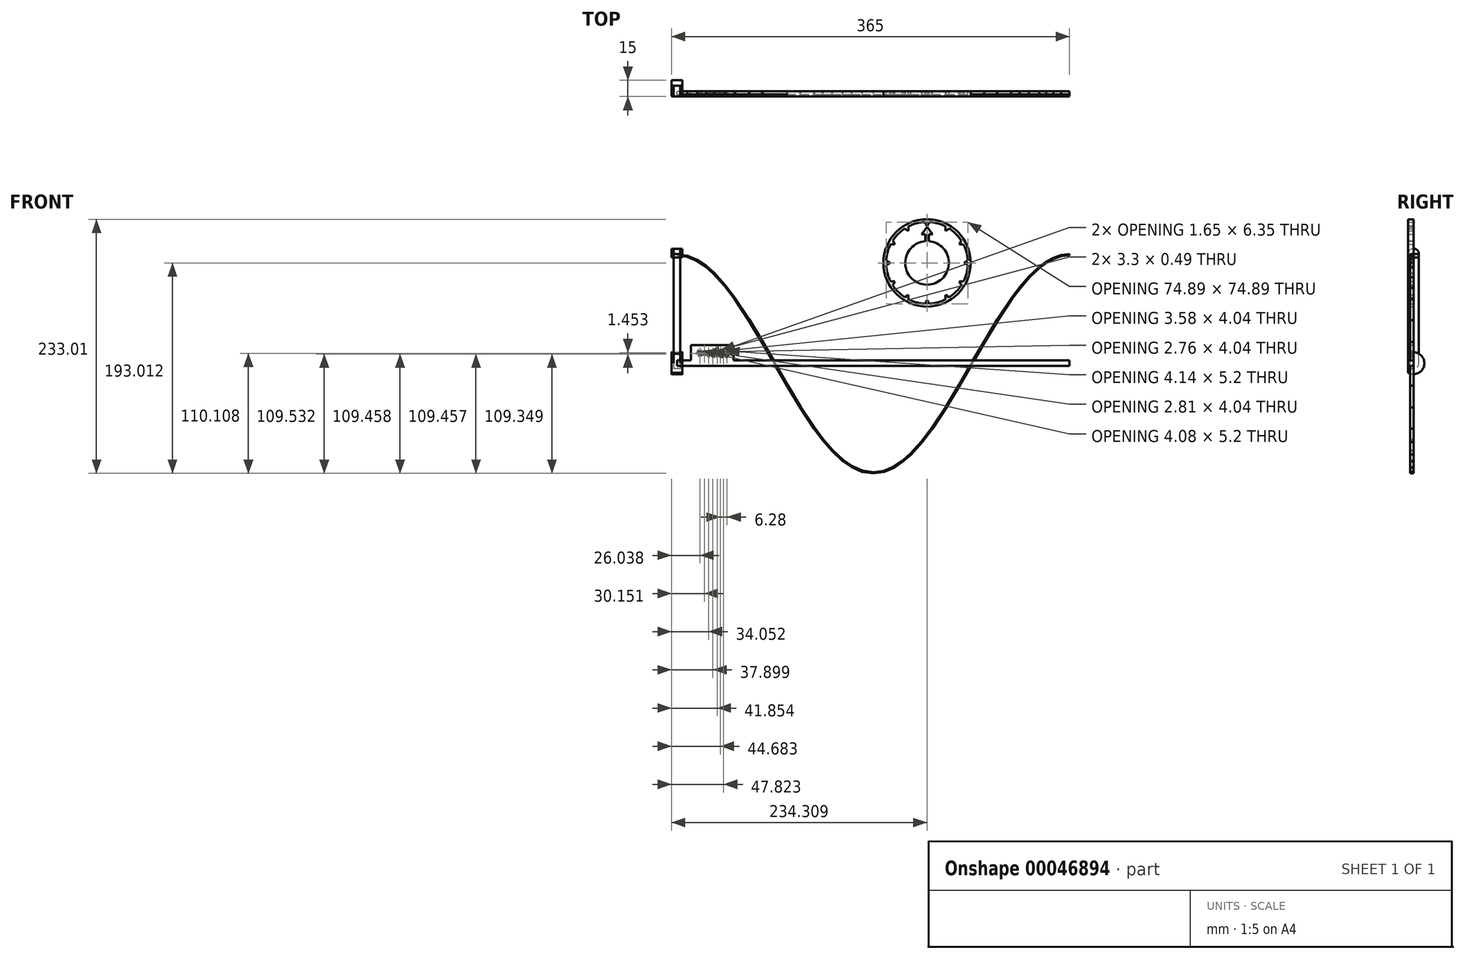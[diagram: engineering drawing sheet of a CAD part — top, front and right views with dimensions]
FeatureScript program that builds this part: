
annotation { "Feature Type Name" : "Feature", "Feature Type Description" : "" }
export const myFeature = defineFeature(function(context is Context, id is Id, definition is map)
    precondition{}
    {
        {
            var Q0;
            Q0=qCreatedBy(makeId("Right.planeOp"),FACE);
            var sketch = newSketch(context, id + "F0", { "sketchPlane" : qUnion([Q0])});
            skArc(sketch, "E0", {"start": v(-5, 0) * mm, "mid": v(0, -5) * mm, "end": v(5, 0) * mm});
            skArc(sketch, "E1", {"start": v(5, 100) * mm, "mid": v(0, 105) * mm, "end": v(-5, 100) * mm});
            skLineSegment(sketch, "E2.left", {"start": v(5, 0) * mm, "end": v(5, 100) * mm});
            skLineSegment(sketch, "E2.right", {"start": v(-5, 0) * mm, "end": v(-5, 100) * mm});
            skSolve(sketch);
        }
        {
            var Q0;
            Q0 = qSketchRegion(id + "F0", true);
            extrude(context, id + "F1", {"entities" : qUnion([Q0]), "endBound" : BoundingType.SYMMETRIC, "depth" : 6 * mm});
        }
        {
            var Q0;
            Q0=qCreatedBy(makeId("Right.planeOp"),FACE);
            var sketch = newSketch(context, id + "F2", { "sketchPlane" : qUnion([Q0])});
            skArc(sketch, "E3", {"start": v(5, 100) * mm, "mid": v(0, 105) * mm, "end": v(-5, 100) * mm});
            skLineSegment(sketch, "E4", {"start": v(5, 100) * mm, "end": v(-5, 100) * mm});
            skSolve(sketch);
        }
        {
            var Q0;
            Q0 = qSketchRegion(id + "F2", true);
            extrude(context, id + "F3", {"entities" : qUnion([Q0]), "endBound" : BoundingType.SYMMETRIC, "depth" : 10 * mm});
        }
        {
            var Q0;
            Q0=qCreatedBy(makeId("Right.planeOp"),FACE);
            var sketch = newSketch(context, id + "F4", { "sketchPlane" : qUnion([Q0])});
            skLineSegment(sketch, "E5.top", {"start": v(5, 97) * mm, "end": v(-5, 97) * mm});
            skLineSegment(sketch, "E5.left", {"start": v(5, 100) * mm, "end": v(5, 97) * mm});
            skLineSegment(sketch, "E5.right", {"start": v(-5, 100) * mm, "end": v(-5, 97) * mm});
            skLineSegment(sketch, "E6", {"start": v(-5, 100) * mm, "end": v(5, 100) * mm});
            skPoint(sketch, "E5.bottom.end.orphan", {"position": v(-5, 103) * mm});
            skPoint(sketch, "E5.bottom.start.orphan", {"position": v(5, 103) * mm});
            skSolve(sketch);
        }
        {
            var Q0;
            Q0 = qSketchRegion(id + "F4", true);
            extrude(context, id + "F5", {"entities" : qUnion([Q0]), "endBound" : BoundingType.SYMMETRIC, "depth" : 10 * mm});
        }
        {
            var Q0;
            Q0=qCreatedBy(makeId("Right.planeOp"),FACE);
            var sketch = newSketch(context, id + "F6", { "sketchPlane" : qUnion([Q0])});
            skArc(sketch, "E7", {"start": v(-5, -8.66) * mm, "mid": v(10, 0) * mm, "end": v(-5, 8.66) * mm});
            skLineSegment(sketch, "E8", {"start": v(-5, 8.66) * mm, "end": v(-5, -8.66) * mm});
            skSolve(sketch);
        }
        {
            var Q0;
            Q0 = qSketchRegion(id + "F6", true);
            extrude(context, id + "F7", {"entities" : qUnion([Q0]), "endBound" : BoundingType.SYMMETRIC, "depth" : 10 * mm});
        }
        {
            var Q0;
            Q0=qCreatedBy(makeId("Front.planeOp"),FACE);
            var sketch = newSketch(context, id + "F8", { "sketchPlane" : qUnion([Q0])});
            skLineSegment(sketch, "E9.bottom", {"start": v(0, 2.5) * mm, "end": v(12.73, 2.5) * mm});
            skLineSegment(sketch, "E9.top", {"start": v(0, -2.5) * mm, "end": v(360, -2.5) * mm});
            skLineSegment(sketch, "E9.left", {"start": v(0, 2.5) * mm, "end": v(0, -2.5) * mm});
            skLineSegment(sketch, "E9.right", {"start": v(360, 2.5) * mm, "end": v(360, -2.5) * mm});
            skLineSegment(sketch, "E10.bottom", {"start": v(12.73, 16.53) * mm, "end": v(51.84, 16.53) * mm});
            skLineSegment(sketch, "E10.left", {"start": v(12.73, 16.53) * mm, "end": v(12.73, 2.5) * mm});
            skLineSegment(sketch, "E10.right", {"start": v(51.84, 16.53) * mm, "end": v(51.84, 2.5) * mm});
            skText(sketch, "E11", { "text": "Y=cos(X)\n", "fontName": "OpenSans-Regular.ttf"});
            skLineSegment(sketch, "E12.trimOffspring", {"start": v(51.84, 2.5) * mm, "end": v(360, 2.5) * mm});
            const initialGuessF8  = {"E11": [0.019, 0.0065, 1, 0, 0.00524]};
            skSetInitialGuess(sketch, initialGuessF8);
            skSolve(sketch);
        }
        {
            var Q0;
            Q0 = qSketchRegion(id + "F8", true);
            extrude(context, id + "F9", {"entities" : qUnion([Q0]), "depth" : 5 * mm});
        }
        {
            var Q0;
            Q0=qCreatedBy(makeId("Front.planeOp"),FACE);
            var sketch = newSketch(context, id + "F10", { "sketchPlane" : qUnion([Q0])});
            skCircle(sketch, "E13", {"center": v(229.3, 92) * mm, "radius": 40 * mm});
            skArc(sketch, "E14", {"start": v(227.32, 129.45) * mm, "mid": v(219.6, 128.22) * mm, "end": v(212.3, 125.43) * mm});
            skLineSegment(sketch, "E15", {"start": v(229.3, 126) * mm, "end": v(231.3, 129.45) * mm});
            skLineSegment(sketch, "E16", {"start": v(229.3, 126) * mm, "end": v(227.32, 129.45) * mm});
            skLineSegment(sketch, "E17", {"start": v(229.3, 126) * mm, "end": v(229.3, 92) * mm, "construction": true});
            skLineSegment(sketch, "E18.1.0", {"start": v(212.3, 121.45) * mm, "end": v(208.86, 123.44) * mm});
            skLineSegment(sketch, "E18.1.1", {"start": v(212.3, 121.45) * mm, "end": v(212.3, 125.43) * mm});
            skLineSegment(sketch, "E18.2.0", {"start": v(199.86, 109) * mm, "end": v(195.88, 109) * mm});
            skLineSegment(sketch, "E18.2.1", {"start": v(199.86, 109) * mm, "end": v(197.87, 112.45) * mm});
            skLineSegment(sketch, "E18.3.0", {"start": v(195.3, 92) * mm, "end": v(191.86, 90.01) * mm});
            skLineSegment(sketch, "E18.3.1", {"start": v(195.3, 92) * mm, "end": v(191.86, 94) * mm});
            skLineSegment(sketch, "E18.4.0", {"start": v(199.86, 75) * mm, "end": v(197.87, 71.56) * mm});
            skLineSegment(sketch, "E18.4.1", {"start": v(199.86, 75) * mm, "end": v(195.88, 75) * mm});
            skLineSegment(sketch, "E18.5.0", {"start": v(212.3, 62.56) * mm, "end": v(212.3, 58.58) * mm});
            skLineSegment(sketch, "E18.5.1", {"start": v(212.3, 62.56) * mm, "end": v(208.86, 60.57) * mm});
            skLineSegment(sketch, "E18.6.0", {"start": v(229.3, 58) * mm, "end": v(231.3, 54.56) * mm});
            skLineSegment(sketch, "E18.6.1", {"start": v(229.3, 58) * mm, "end": v(227.32, 54.56) * mm});
            skLineSegment(sketch, "E18.7.0", {"start": v(246.3, 62.56) * mm, "end": v(249.76, 60.57) * mm});
            skLineSegment(sketch, "E18.7.1", {"start": v(246.3, 62.56) * mm, "end": v(246.3, 58.58) * mm});
            skLineSegment(sketch, "E18.8.0", {"start": v(258.75, 75) * mm, "end": v(262.73, 75) * mm});
            skLineSegment(sketch, "E18.8.1", {"start": v(258.75, 75) * mm, "end": v(260.74, 71.56) * mm});
            skLineSegment(sketch, "E18.9.0", {"start": v(263.3, 92) * mm, "end": v(266.76, 94) * mm});
            skLineSegment(sketch, "E18.9.1", {"start": v(263.3, 92) * mm, "end": v(266.76, 90.01) * mm});
            skLineSegment(sketch, "E18.10.0", {"start": v(258.75, 109) * mm, "end": v(260.74, 112.45) * mm});
            skLineSegment(sketch, "E18.10.1", {"start": v(258.75, 109) * mm, "end": v(262.73, 109) * mm});
            skLineSegment(sketch, "E18.11.0", {"start": v(246.3, 121.45) * mm, "end": v(246.3, 125.43) * mm});
            skLineSegment(sketch, "E18.11.1", {"start": v(246.3, 121.45) * mm, "end": v(249.76, 123.44) * mm});
            skArc(sketch, "E19.trimOffspring", {"start": v(208.86, 123.44) * mm, "mid": v(202.8, 118.52) * mm, "end": v(197.87, 112.45) * mm});
            skArc(sketch, "E20.trimOffspring", {"start": v(246.3, 125.43) * mm, "mid": v(239.01, 128.22) * mm, "end": v(231.3, 129.45) * mm});
            skArc(sketch, "E21.trimOffspring", {"start": v(260.74, 112.45) * mm, "mid": v(255.83, 118.52) * mm, "end": v(249.76, 123.44) * mm});
            skArc(sketch, "E22.trimOffspring", {"start": v(195.88, 109) * mm, "mid": v(193.09, 101.7) * mm, "end": v(191.86, 94) * mm});
            skArc(sketch, "E23.trimOffspring", {"start": v(191.86, 90.01) * mm, "mid": v(193.09, 82.3) * mm, "end": v(195.88, 75) * mm});
            skArc(sketch, "E24.trimOffspring", {"start": v(266.76, 94) * mm, "mid": v(265.53, 101.7) * mm, "end": v(262.73, 109) * mm});
            skArc(sketch, "E25.trimOffspring", {"start": v(262.73, 75) * mm, "mid": v(265.53, 82.3) * mm, "end": v(266.76, 90.01) * mm});
            skArc(sketch, "E26.trimOffspring", {"start": v(249.76, 60.57) * mm, "mid": v(255.83, 65.49) * mm, "end": v(260.74, 71.56) * mm});
            skArc(sketch, "E27.trimOffspring", {"start": v(231.3, 54.56) * mm, "mid": v(239.01, 55.78) * mm, "end": v(246.3, 58.58) * mm});
            skArc(sketch, "E28.trimOffspring", {"start": v(212.3, 58.58) * mm, "mid": v(219.6, 55.78) * mm, "end": v(227.32, 54.56) * mm});
            skArc(sketch, "E29.trimOffspring", {"start": v(197.87, 71.56) * mm, "mid": v(202.8, 65.49) * mm, "end": v(208.86, 60.57) * mm});
            skLineSegment(sketch, "E30.left", {"start": v(227.8, 111.95) * mm, "end": v(227.8, 118.11) * mm});
            skLineSegment(sketch, "E30.right", {"start": v(230.8, 111.95) * mm, "end": v(230.8, 118.11) * mm});
            skLineSegment(sketch, "E31", {"start": v(229.3, 125) * mm, "end": v(224.3, 118.11) * mm});
            skLineSegment(sketch, "E32", {"start": v(224.3, 118.11) * mm, "end": v(227.8, 118.11) * mm});
            skLineSegment(sketch, "E33", {"start": v(234.3, 118.11) * mm, "end": v(229.3, 125) * mm});
            skLineSegment(sketch, "E34.trimOffspring", {"start": v(230.8, 118.11) * mm, "end": v(234.3, 118.11) * mm});
            skArc(sketch, "E35", {"start": v(227.8, 111.95) * mm, "mid": v(229.3, 72) * mm, "end": v(230.8, 111.95) * mm});
            skSolve(sketch);
        }
        {
            var Q0;
            Q0 = qSketchRegion(id + "F10", true);
            var Q1;
            Q1=makeQuery(id+"F10.imprint","IMPRINT",FACE,{"disambiguationData":[TD([[makeQuery(id+"F10.imprint","IMPRINT",EDGE,{"derivedFrom":sQuery(id+"F10.wireOp",EDGE,"E30.left")}),-1.0]])]});
            extrude(context, id + "F11", {"entities" : qUnion([Q0, Q1]), "depth" : 5 * mm});
        }
        {
            var Q0;
            Q0=qCreatedBy(makeId("Front.planeOp"),FACE);
            var sketch = newSketch(context, id + "F12", { "sketchPlane" : qUnion([Q0])});
            skLineSegment(sketch, "E36", {"start": v(30.91, -2.55) * mm, "end": v(90.38, -2.55) * mm});
            skLineSegment(sketch, "E37", {"start": v(30.91, 97.45) * mm, "end": v(40.53, 96.04) * mm});
            skLineSegment(sketch, "E38", {"start": v(40.53, 96.04) * mm, "end": v(49.5, 92.24) * mm});
            skLineSegment(sketch, "E39", {"start": v(49.5, 92.24) * mm, "end": v(57.58, 86.8) * mm});
            skLineSegment(sketch, "E40", {"start": v(57.58, 86.8) * mm, "end": v(64.9, 80.36) * mm});
            skLineSegment(sketch, "E41", {"start": v(64.9, 80.36) * mm, "end": v(75.2, 69.02) * mm});
            skLineSegment(sketch, "E42", {"start": v(75.2, 69.02) * mm, "end": v(84.49, 56.82) * mm});
            skLineSegment(sketch, "E43", {"start": v(84.49, 56.82) * mm, "end": v(97.32, 37.47) * mm});
            skLineSegment(sketch, "E44", {"start": v(97.32, 37.47) * mm, "end": v(109.3, 17.57) * mm});
            skLineSegment(sketch, "E45", {"start": v(109.3, 17.57) * mm, "end": v(120.91, -2.55) * mm});
            skLineSegment(sketch, "E46", {"start": v(120.91, -2.55) * mm, "end": v(132.52, -22.67) * mm});
            skLineSegment(sketch, "E47", {"start": v(132.52, -22.67) * mm, "end": v(144.5, -42.57) * mm});
            skLineSegment(sketch, "E48", {"start": v(144.5, -42.57) * mm, "end": v(157.33, -61.92) * mm});
            skLineSegment(sketch, "E49", {"start": v(157.33, -61.92) * mm, "end": v(165.15, -72.32) * mm});
            skLineSegment(sketch, "E50", {"start": v(165.15, -72.32) * mm, "end": v(173.66, -82.15) * mm});
            skLineSegment(sketch, "E51", {"start": v(173.66, -82.15) * mm, "end": v(183.15, -91.04) * mm});
            skLineSegment(sketch, "E52", {"start": v(183.15, -91.04) * mm, "end": v(191.52, -96.88) * mm});
            skLineSegment(sketch, "E53", {"start": v(191.52, -96.88) * mm, "end": v(200.84, -101.01) * mm});
            skLineSegment(sketch, "E54", {"start": v(200.84, -101.01) * mm, "end": v(210.91, -102.55) * mm});
            skLineSegment(sketch, "E55", {"start": v(210.91, -102.55) * mm, "end": v(220.53, -101.14) * mm});
            skLineSegment(sketch, "E56", {"start": v(220.53, -101.14) * mm, "end": v(229.5, -97.34) * mm});
            skLineSegment(sketch, "E57", {"start": v(229.5, -97.34) * mm, "end": v(237.58, -91.9) * mm});
            skLineSegment(sketch, "E58", {"start": v(237.58, -91.9) * mm, "end": v(244.9, -85.46) * mm});
            skLineSegment(sketch, "E59", {"start": v(244.9, -85.46) * mm, "end": v(255.2, -74.12) * mm});
            skLineSegment(sketch, "E60", {"start": v(255.2, -74.12) * mm, "end": v(264.49, -61.92) * mm});
            skLineSegment(sketch, "E61", {"start": v(264.49, -61.92) * mm, "end": v(277.32, -42.57) * mm});
            skLineSegment(sketch, "E62", {"start": v(277.32, -42.57) * mm, "end": v(289.3, -22.67) * mm});
            skLineSegment(sketch, "E63", {"start": v(289.3, -22.67) * mm, "end": v(300.91, -2.55) * mm});
            skLineSegment(sketch, "E64", {"start": v(300.91, -2.55) * mm, "end": v(312.52, 17.57) * mm});
            skLineSegment(sketch, "E65", {"start": v(312.52, 17.57) * mm, "end": v(324.5, 37.47) * mm});
            skLineSegment(sketch, "E66", {"start": v(324.5, 37.47) * mm, "end": v(337.33, 56.82) * mm});
            skLineSegment(sketch, "E67", {"start": v(337.33, 56.82) * mm, "end": v(345.15, 67.22) * mm});
            skLineSegment(sketch, "E68", {"start": v(345.15, 67.22) * mm, "end": v(353.66, 77.05) * mm});
            skLineSegment(sketch, "E69", {"start": v(353.66, 77.05) * mm, "end": v(363.15, 85.94) * mm});
            skLineSegment(sketch, "E70", {"start": v(363.15, 85.94) * mm, "end": v(369.34, 90.45) * mm});
            skLineSegment(sketch, "E71", {"start": v(369.34, 90.45) * mm, "end": v(376.07, 94.11) * mm});
            skLineSegment(sketch, "E72", {"start": v(376.07, 94.11) * mm, "end": v(383.31, 96.57) * mm});
            skLineSegment(sketch, "E73", {"start": v(383.31, 96.57) * mm, "end": v(390.91, 97.45) * mm});
            skPoint(sketch, "E74", {"position": v(0, 0) * mm});
            skLineSegment(sketch, "E75", {"start": v(30.91, 97.45) * mm, "end": v(30.91, -2.55) * mm});
            skLineSegment(sketch, "E76", {"start": v(390.91, -2.55) * mm, "end": v(390.91, 97.45) * mm});
            skLineSegment(sketch, "E77.top", {"start": v(90.38, -123.52) * mm, "end": v(342.91, -123.52) * mm});
            skLineSegment(sketch, "E77.left", {"start": v(90.38, -2.55) * mm, "end": v(90.38, -123.52) * mm});
            skLineSegment(sketch, "E77.right", {"start": v(342.91, -2.55) * mm, "end": v(342.91, -123.52) * mm});
            skLineSegment(sketch, "E78.trimOffspring", {"start": v(342.91, -2.55) * mm, "end": v(390.91, -2.55) * mm});
            skSolve(sketch);
        }
        {
            var Q0;
            Q0 = qSketchRegion(id + "F12", true);
            extrude(context, id + "F13", {"entities" : qUnion([Q0]), "depth" : 3 * mm});
        }
        {
            var Q0;
            Q0=makeQuery(id+"F13.opExtrude","SWEPT_BODY",BODY,{"disambiguationData":[OSD([sQuery(id+"F12.wireOp",EDGE,"E36"),sQuery(id+"F12.wireOp",EDGE,"E37"),sQuery(id+"F12.wireOp",EDGE,"E38"),sQuery(id+"F12.wireOp",EDGE,"E39"),sQuery(id+"F12.wireOp",EDGE,"E40"),sQuery(id+"F12.wireOp",EDGE,"E41"),sQuery(id+"F12.wireOp",EDGE,"E42"),sQuery(id+"F12.wireOp",EDGE,"E43"),sQuery(id+"F12.wireOp",EDGE,"E44"),sQuery(id+"F12.wireOp",EDGE,"E45"),sQuery(id+"F12.wireOp",EDGE,"E46"),sQuery(id+"F12.wireOp",EDGE,"E47"),sQuery(id+"F12.wireOp",EDGE,"E48"),sQuery(id+"F12.wireOp",EDGE,"E49"),sQuery(id+"F12.wireOp",EDGE,"E50"),sQuery(id+"F12.wireOp",EDGE,"E51"),sQuery(id+"F12.wireOp",EDGE,"E52"),sQuery(id+"F12.wireOp",EDGE,"E53"),sQuery(id+"F12.wireOp",EDGE,"E54"),sQuery(id+"F12.wireOp",EDGE,"E55"),sQuery(id+"F12.wireOp",EDGE,"E56"),sQuery(id+"F12.wireOp",EDGE,"E57"),sQuery(id+"F12.wireOp",EDGE,"E58"),sQuery(id+"F12.wireOp",EDGE,"E59"),sQuery(id+"F12.wireOp",EDGE,"E60"),sQuery(id+"F12.wireOp",EDGE,"E61"),sQuery(id+"F12.wireOp",EDGE,"E62"),sQuery(id+"F12.wireOp",EDGE,"E63"),sQuery(id+"F12.wireOp",EDGE,"E64"),sQuery(id+"F12.wireOp",EDGE,"E65"),sQuery(id+"F12.wireOp",EDGE,"E66"),sQuery(id+"F12.wireOp",EDGE,"E67"),sQuery(id+"F12.wireOp",EDGE,"E68"),sQuery(id+"F12.wireOp",EDGE,"E69"),sQuery(id+"F12.wireOp",EDGE,"E70"),sQuery(id+"F12.wireOp",EDGE,"E71"),sQuery(id+"F12.wireOp",EDGE,"E72"),sQuery(id+"F12.wireOp",EDGE,"E73"),sQuery(id+"F12.wireOp",EDGE,"E75"),sQuery(id+"F12.wireOp",EDGE,"E76"),sQuery(id+"F12.wireOp",EDGE,"E77.top"),sQuery(id+"F12.wireOp",EDGE,"E77.left"),sQuery(id+"F12.wireOp",EDGE,"E77.right"),sQuery(id+"F12.wireOp",EDGE,"E78.trimOffspring")])]});
            var Q1;
            Q1=makeQuery(id+"F13.opExtrude","CAP_VERTEX",VERTEX,{"disambiguationData":[OSD([sQuery(id+"F12.wireOp",EDGE,"E36"),sQuery(id+"F12.wireOp",EDGE,"E75")])],"isStart":true});
            var Q2;
            Q2=qCreatedBy(makeId("Origin.pointOp"),VERTEX);
            var Q3;
            Q3=makeQuery(id+"F13.opExtrude","CAP_VERTEX",VERTEX,{"disambiguationData":[OSD([sQuery(id+"F12.wireOp",EDGE,"E36"),sQuery(id+"F12.wireOp",EDGE,"E75")])],"isStart":true});
            var Q4;
            Q4=qCreatedBy(makeId("Origin.pointOp"),VERTEX);
            transform(context, id + "F14", {"entities" : qUnion([Q0]), "transformType" : TransformType.TRANSLATION_ENTITY, "oppositeDirectionEntity" : false, "transformLine" : qUnion([Q1, Q2]), "makeCopy" : false});
        }
        {
            var Q0;
            Q0=makeQuery(id+"F13.opExtrude","SWEPT_FACE",FACE,{"disambiguationData":[OSD([sQuery(id+"F12.wireOp",EDGE,"E77.top")])]});
            var Q1;
            Q1=makeQuery(id+"F13.opExtrude","SWEPT_FACE",FACE,{"disambiguationData":[OSD([sQuery(id+"F12.wireOp",EDGE,"E36")])]});
            var Q2;
            Q2=makeQuery(id+"F13.opExtrude","CAP_FACE",FACE,{"disambiguationData":[OSD([sQuery(id+"F12.wireOp",EDGE,"E36"),sQuery(id+"F12.wireOp",EDGE,"E37"),sQuery(id+"F12.wireOp",EDGE,"E38"),sQuery(id+"F12.wireOp",EDGE,"E39"),sQuery(id+"F12.wireOp",EDGE,"E40"),sQuery(id+"F12.wireOp",EDGE,"E41"),sQuery(id+"F12.wireOp",EDGE,"E42"),sQuery(id+"F12.wireOp",EDGE,"E43"),sQuery(id+"F12.wireOp",EDGE,"E44"),sQuery(id+"F12.wireOp",EDGE,"E45"),sQuery(id+"F12.wireOp",EDGE,"E46"),sQuery(id+"F12.wireOp",EDGE,"E47"),sQuery(id+"F12.wireOp",EDGE,"E48"),sQuery(id+"F12.wireOp",EDGE,"E49"),sQuery(id+"F12.wireOp",EDGE,"E50"),sQuery(id+"F12.wireOp",EDGE,"E51"),sQuery(id+"F12.wireOp",EDGE,"E52"),sQuery(id+"F12.wireOp",EDGE,"E53"),sQuery(id+"F12.wireOp",EDGE,"E54"),sQuery(id+"F12.wireOp",EDGE,"E55"),sQuery(id+"F12.wireOp",EDGE,"E56"),sQuery(id+"F12.wireOp",EDGE,"E57"),sQuery(id+"F12.wireOp",EDGE,"E58"),sQuery(id+"F12.wireOp",EDGE,"E59"),sQuery(id+"F12.wireOp",EDGE,"E60"),sQuery(id+"F12.wireOp",EDGE,"E61"),sQuery(id+"F12.wireOp",EDGE,"E62"),sQuery(id+"F12.wireOp",EDGE,"E63"),sQuery(id+"F12.wireOp",EDGE,"E64"),sQuery(id+"F12.wireOp",EDGE,"E65"),sQuery(id+"F12.wireOp",EDGE,"E66"),sQuery(id+"F12.wireOp",EDGE,"E67"),sQuery(id+"F12.wireOp",EDGE,"E68"),sQuery(id+"F12.wireOp",EDGE,"E69"),sQuery(id+"F12.wireOp",EDGE,"E70"),sQuery(id+"F12.wireOp",EDGE,"E71"),sQuery(id+"F12.wireOp",EDGE,"E72"),sQuery(id+"F12.wireOp",EDGE,"E73"),sQuery(id+"F12.wireOp",EDGE,"E75"),sQuery(id+"F12.wireOp",EDGE,"E76"),sQuery(id+"F12.wireOp",EDGE,"E77.top"),sQuery(id+"F12.wireOp",EDGE,"E77.left"),sQuery(id+"F12.wireOp",EDGE,"E77.right"),sQuery(id+"F12.wireOp",EDGE,"E78.trimOffspring")])],"isStart":false});
            var Q3;
            Q3=makeQuery(id+"F13.opExtrude","SWEPT_FACE",FACE,{"disambiguationData":[OSD([sQuery(id+"F12.wireOp",EDGE,"E77.left")])]});
            var Q4;
            Q4=makeQuery(id+"F13.opExtrude","SWEPT_FACE",FACE,{"disambiguationData":[OSD([sQuery(id+"F12.wireOp",EDGE,"E75")])]});
            var Q5;
            Q5=makeQuery(id+"F13.opExtrude","SWEPT_FACE",FACE,{"disambiguationData":[OSD([sQuery(id+"F12.wireOp",EDGE,"E77.right")])]});
            var Q6;
            Q6=makeQuery(id+"F13.opExtrude","SWEPT_FACE",FACE,{"disambiguationData":[OSD([sQuery(id+"F12.wireOp",EDGE,"E78.trimOffspring")])]});
            var Q7;
            Q7=makeQuery(id+"F13.opExtrude","SWEPT_FACE",FACE,{"disambiguationData":[OSD([sQuery(id+"F12.wireOp",EDGE,"E76")])]});
            var Q8;
            Q8=makeQuery(id+"F13.opExtrude","CAP_FACE",FACE,{"disambiguationData":[OSD([sQuery(id+"F12.wireOp",EDGE,"E36"),sQuery(id+"F12.wireOp",EDGE,"E37"),sQuery(id+"F12.wireOp",EDGE,"E38"),sQuery(id+"F12.wireOp",EDGE,"E39"),sQuery(id+"F12.wireOp",EDGE,"E40"),sQuery(id+"F12.wireOp",EDGE,"E41"),sQuery(id+"F12.wireOp",EDGE,"E42"),sQuery(id+"F12.wireOp",EDGE,"E43"),sQuery(id+"F12.wireOp",EDGE,"E44"),sQuery(id+"F12.wireOp",EDGE,"E45"),sQuery(id+"F12.wireOp",EDGE,"E46"),sQuery(id+"F12.wireOp",EDGE,"E47"),sQuery(id+"F12.wireOp",EDGE,"E48"),sQuery(id+"F12.wireOp",EDGE,"E49"),sQuery(id+"F12.wireOp",EDGE,"E50"),sQuery(id+"F12.wireOp",EDGE,"E51"),sQuery(id+"F12.wireOp",EDGE,"E52"),sQuery(id+"F12.wireOp",EDGE,"E53"),sQuery(id+"F12.wireOp",EDGE,"E54"),sQuery(id+"F12.wireOp",EDGE,"E55"),sQuery(id+"F12.wireOp",EDGE,"E56"),sQuery(id+"F12.wireOp",EDGE,"E57"),sQuery(id+"F12.wireOp",EDGE,"E58"),sQuery(id+"F12.wireOp",EDGE,"E59"),sQuery(id+"F12.wireOp",EDGE,"E60"),sQuery(id+"F12.wireOp",EDGE,"E61"),sQuery(id+"F12.wireOp",EDGE,"E62"),sQuery(id+"F12.wireOp",EDGE,"E63"),sQuery(id+"F12.wireOp",EDGE,"E64"),sQuery(id+"F12.wireOp",EDGE,"E65"),sQuery(id+"F12.wireOp",EDGE,"E66"),sQuery(id+"F12.wireOp",EDGE,"E67"),sQuery(id+"F12.wireOp",EDGE,"E68"),sQuery(id+"F12.wireOp",EDGE,"E69"),sQuery(id+"F12.wireOp",EDGE,"E70"),sQuery(id+"F12.wireOp",EDGE,"E71"),sQuery(id+"F12.wireOp",EDGE,"E72"),sQuery(id+"F12.wireOp",EDGE,"E73"),sQuery(id+"F12.wireOp",EDGE,"E75"),sQuery(id+"F12.wireOp",EDGE,"E76"),sQuery(id+"F12.wireOp",EDGE,"E77.top"),sQuery(id+"F12.wireOp",EDGE,"E77.left"),sQuery(id+"F12.wireOp",EDGE,"E77.right"),sQuery(id+"F12.wireOp",EDGE,"E78.trimOffspring")])],"isStart":true});
            shell(context, id + "F15", {"entities" : qUnion([Q0, Q1, Q2, Q3, Q4, Q5, Q6, Q7, Q8]), "thickness" : 1 * mm});
        }
        {
            var Q0;
            Q0=makeQuery(id+"F9.opExtrude","CAP_FACE",FACE,{"disambiguationData":[OSD([sQuery(id+"F8.wireOp",EDGE,"E9.bottom"),sQuery(id+"F8.wireOp",EDGE,"E9.top"),sQuery(id+"F8.wireOp",EDGE,"E9.left"),sQuery(id+"F8.wireOp",EDGE,"E9.right"),sQuery(id+"F8.wireOp",EDGE,"E10.bottom"),sQuery(id+"F8.wireOp",EDGE,"E10.left"),sQuery(id+"F8.wireOp",EDGE,"E10.right"),sQuery(id+"F8.wireOp",EDGE,"E11.sketch_text.stroke-0"),sQuery(id+"F8.wireOp",EDGE,"E11.sketch_text.stroke-1"),sQuery(id+"F8.wireOp",EDGE,"E11.sketch_text.stroke-2"),sQuery(id+"F8.wireOp",EDGE,"E11.sketch_text.stroke-3"),sQuery(id+"F8.wireOp",EDGE,"E11.sketch_text.stroke-4"),sQuery(id+"F8.wireOp",EDGE,"E11.sketch_text.stroke-5"),sQuery(id+"F8.wireOp",EDGE,"E11.sketch_text.stroke-6"),sQuery(id+"F8.wireOp",EDGE,"E11.sketch_text.stroke-7"),sQuery(id+"F8.wireOp",EDGE,"E11.sketch_text.stroke-8"),sQuery(id+"F8.wireOp",EDGE,"E11.sketch_text.stroke-9"),sQuery(id+"F8.wireOp",EDGE,"E11.sketch_text.stroke-10"),sQuery(id+"F8.wireOp",EDGE,"E11.sketch_text.stroke-11"),sQuery(id+"F8.wireOp",EDGE,"E11.sketch_text.stroke-12"),sQuery(id+"F8.wireOp",EDGE,"E11.sketch_text.stroke-13"),sQuery(id+"F8.wireOp",EDGE,"E11.sketch_text.stroke-14"),sQuery(id+"F8.wireOp",EDGE,"E11.sketch_text.stroke-15"),sQuery(id+"F8.wireOp",EDGE,"E11.sketch_text.stroke-16"),sQuery(id+"F8.wireOp",EDGE,"E11.sketch_text.stroke-17"),sQuery(id+"F8.wireOp",EDGE,"E11.sketch_text.stroke-18"),sQuery(id+"F8.wireOp",EDGE,"E11.sketch_text.stroke-19"),sQuery(id+"F8.wireOp",EDGE,"E11.sketch_text.stroke-20"),sQuery(id+"F8.wireOp",EDGE,"E11.sketch_text.stroke-21"),sQuery(id+"F8.wireOp",EDGE,"E11.sketch_text.stroke-22"),sQuery(id+"F8.wireOp",EDGE,"E11.sketch_text.stroke-23"),sQuery(id+"F8.wireOp",EDGE,"E11.sketch_text.stroke-24"),sQuery(id+"F8.wireOp",EDGE,"E11.sketch_text.stroke-25"),sQuery(id+"F8.wireOp",EDGE,"E11.sketch_text.stroke-26"),sQuery(id+"F8.wireOp",EDGE,"E11.sketch_text.stroke-27"),sQuery(id+"F8.wireOp",EDGE,"E11.sketch_text.stroke-28"),sQuery(id+"F8.wireOp",EDGE,"E11.sketch_text.stroke-29"),sQuery(id+"F8.wireOp",EDGE,"E11.sketch_text.stroke-30"),sQuery(id+"F8.wireOp",EDGE,"E11.sketch_text.stroke-31"),sQuery(id+"F8.wireOp",EDGE,"E11.sketch_text.stroke-32"),sQuery(id+"F8.wireOp",EDGE,"E11.sketch_text.stroke-33"),sQuery(id+"F8.wireOp",EDGE,"E11.sketch_text.stroke-34"),sQuery(id+"F8.wireOp",EDGE,"E11.sketch_text.stroke-35"),sQuery(id+"F8.wireOp",EDGE,"E11.sketch_text.stroke-36"),sQuery(id+"F8.wireOp",EDGE,"E11.sketch_text.stroke-37"),sQuery(id+"F8.wireOp",EDGE,"E11.sketch_text.stroke-38"),sQuery(id+"F8.wireOp",EDGE,"E11.sketch_text.stroke-39"),sQuery(id+"F8.wireOp",EDGE,"E11.sketch_text.stroke-40"),sQuery(id+"F8.wireOp",EDGE,"E11.sketch_text.stroke-49"),sQuery(id+"F8.wireOp",EDGE,"E11.sketch_text.stroke-50"),sQuery(id+"F8.wireOp",EDGE,"E11.sketch_text.stroke-51"),sQuery(id+"F8.wireOp",EDGE,"E11.sketch_text.stroke-52"),sQuery(id+"F8.wireOp",EDGE,"E11.sketch_text.stroke-53"),sQuery(id+"F8.wireOp",EDGE,"E11.sketch_text.stroke-54"),sQuery(id+"F8.wireOp",EDGE,"E11.sketch_text.stroke-55"),sQuery(id+"F8.wireOp",EDGE,"E11.sketch_text.stroke-56"),sQuery(id+"F8.wireOp",EDGE,"E11.sketch_text.stroke-57"),sQuery(id+"F8.wireOp",EDGE,"E11.sketch_text.stroke-58"),sQuery(id+"F8.wireOp",EDGE,"E11.sketch_text.stroke-59"),sQuery(id+"F8.wireOp",EDGE,"E11.sketch_text.stroke-60"),sQuery(id+"F8.wireOp",EDGE,"E11.sketch_text.stroke-61"),sQuery(id+"F8.wireOp",EDGE,"E11.sketch_text.stroke-62"),sQuery(id+"F8.wireOp",EDGE,"E11.sketch_text.stroke-63"),sQuery(id+"F8.wireOp",EDGE,"E11.sketch_text.stroke-64"),sQuery(id+"F8.wireOp",EDGE,"E11.sketch_text.stroke-65"),sQuery(id+"F8.wireOp",EDGE,"E11.sketch_text.stroke-66"),sQuery(id+"F8.wireOp",EDGE,"E11.sketch_text.stroke-67"),sQuery(id+"F8.wireOp",EDGE,"E11.sketch_text.stroke-68"),sQuery(id+"F8.wireOp",EDGE,"E11.sketch_text.stroke-69"),sQuery(id+"F8.wireOp",EDGE,"E11.sketch_text.stroke-70"),sQuery(id+"F8.wireOp",EDGE,"E11.sketch_text.stroke-71"),sQuery(id+"F8.wireOp",EDGE,"E11.sketch_text.stroke-72"),sQuery(id+"F8.wireOp",EDGE,"E11.sketch_text.stroke-73"),sQuery(id+"F8.wireOp",EDGE,"E11.sketch_text.stroke-74"),sQuery(id+"F8.wireOp",EDGE,"E11.sketch_text.stroke-75"),sQuery(id+"F8.wireOp",EDGE,"E11.sketch_text.stroke-76"),sQuery(id+"F8.wireOp",EDGE,"E11.sketch_text.stroke-77"),sQuery(id+"F8.wireOp",EDGE,"E11.sketch_text.stroke-78"),sQuery(id+"F8.wireOp",EDGE,"E11.sketch_text.stroke-79"),sQuery(id+"F8.wireOp",EDGE,"E11.sketch_text.stroke-80"),sQuery(id+"F8.wireOp",EDGE,"E11.sketch_text.stroke-81"),sQuery(id+"F8.wireOp",EDGE,"E11.sketch_text.stroke-82"),sQuery(id+"F8.wireOp",EDGE,"E11.sketch_text.stroke-83"),sQuery(id+"F8.wireOp",EDGE,"E11.sketch_text.stroke-84"),sQuery(id+"F8.wireOp",EDGE,"E11.sketch_text.stroke-85"),sQuery(id+"F8.wireOp",EDGE,"E11.sketch_text.stroke-86"),sQuery(id+"F8.wireOp",EDGE,"E11.sketch_text.stroke-87"),sQuery(id+"F8.wireOp",EDGE,"E11.sketch_text.stroke-88"),sQuery(id+"F8.wireOp",EDGE,"E11.sketch_text.stroke-89"),sQuery(id+"F8.wireOp",EDGE,"E11.sketch_text.stroke-90"),sQuery(id+"F8.wireOp",EDGE,"E11.sketch_text.stroke-91"),sQuery(id+"F8.wireOp",EDGE,"E11.sketch_text.stroke-92"),sQuery(id+"F8.wireOp",EDGE,"E11.sketch_text.stroke-93"),sQuery(id+"F8.wireOp",EDGE,"E11.sketch_text.stroke-94"),sQuery(id+"F8.wireOp",EDGE,"E11.sketch_text.stroke-95"),sQuery(id+"F8.wireOp",EDGE,"E11.sketch_text.stroke-96"),sQuery(id+"F8.wireOp",EDGE,"E11.sketch_text.stroke-97"),sQuery(id+"F8.wireOp",EDGE,"E11.sketch_text.stroke-98"),sQuery(id+"F8.wireOp",EDGE,"E11.sketch_text.stroke-99"),sQuery(id+"F8.wireOp",EDGE,"E11.sketch_text.stroke-100"),sQuery(id+"F8.wireOp",EDGE,"E11.sketch_text.stroke-101"),sQuery(id+"F8.wireOp",EDGE,"E11.sketch_text.stroke-102"),sQuery(id+"F8.wireOp",EDGE,"E11.sketch_text.stroke-103"),sQuery(id+"F8.wireOp",EDGE,"E11.sketch_text.stroke-104"),sQuery(id+"F8.wireOp",EDGE,"E11.sketch_text.stroke-105"),sQuery(id+"F8.wireOp",EDGE,"E12.trimOffspring")])],"isStart":false});
            var sketch = newSketch(context, id + "F16", { "sketchPlane" : qUnion([Q0])});
            skFitSpline(sketch, "E79.0", {"points": [v(31.6, 8.45) * mm, v(31.6, 8.73) * mm, v(31.67, 9.19) * mm, v(31.84, 9.48) * mm, v(31.95, 9.6) * mm]});
            skFitSpline(sketch, "E79.1", {"points": [v(31.77, 7.6) * mm, v(31.66, 7.82) * mm, v(31.6, 8.1) * mm, v(31.6, 8.45) * mm]});
            skFitSpline(sketch, "E79.2", {"points": [v(31.95, 9.6) * mm, v(32.06, 9.73) * mm, v(32.3, 9.9) * mm, v(32.67, 9.97) * mm, v(32.9, 9.97) * mm]});
            skFitSpline(sketch, "E79.3", {"points": [v(32.2, 7.1) * mm, v(32.11, 7.16) * mm, v(31.95, 7.29) * mm, v(31.83, 7.48) * mm, v(31.77, 7.6) * mm]});
            skFitSpline(sketch, "E79.4", {"points": [v(32.88, 6.93) * mm, v(32.74, 6.93) * mm, v(32.5, 6.96) * mm, v(32.3, 7.04) * mm, v(32.2, 7.1) * mm]});
            skFitSpline(sketch, "E79.5", {"points": [v(32.9, 9.97) * mm, v(33.12, 9.97) * mm, v(33.47, 9.9) * mm, v(33.71, 9.72) * mm, v(33.83, 9.6) * mm]});
            skFitSpline(sketch, "E79.6", {"points": [v(33.83, 9.6) * mm, v(33.94, 9.46) * mm, v(34.11, 9.17) * mm, v(34.18, 8.72) * mm, v(34.18, 8.45) * mm]});
            skFitSpline(sketch, "E79.7", {"points": [v(34.18, 8.45) * mm, v(34.18, 8.18) * mm, v(34.11, 7.71) * mm, v(33.94, 7.42) * mm, v(33.83, 7.3) * mm]});
            skFitSpline(sketch, "E79.8", {"points": [v(33.83, 7.3) * mm, v(33.72, 7.17) * mm, v(33.48, 7) * mm, v(33.1, 6.93) * mm, v(32.88, 6.93) * mm]});
            skLineSegment(sketch, "E80.bottom", {"start": v(32.6, 10.65) * mm, "end": v(33.2, 10.65) * mm});
            skLineSegment(sketch, "E80.left", {"start": v(32.6, 10.65) * mm, "end": v(32.6, 9.95) * mm});
            skLineSegment(sketch, "E80.right", {"start": v(33.2, 10.65) * mm, "end": v(33.2, 9.94) * mm});
            skSolve(sketch);
        }
        {
            var Q0;
            Q0=makeQuery(id+"F16.imprint","IMPRINT",FACE,{"disambiguationData":[TD([[makeQuery(id+"F16.imprint","IMPRINT",EDGE,{"derivedFrom":sQuery(id+"F16.wireOp",EDGE,"E79.0")}),-1.0]])]});
            var Q1;
            {var subQ0=sQuery(id+"F16.wireOp",EDGE,"E80.bottom");Q1=makeQuery(id+"F16.imprint","IMPRINT",FACE,{"disambiguationData":[TD([[makeQuery(id+"F16.imprint","IMPRINT",EDGE,{"derivedFrom":subQ0}),-1.0]])]});}
            extrude(context, id + "F17", {"entities" : qUnion([Q0, Q1]), "operationType" : NewBodyOperationType.ADD, "oppositeDirection" : true, "depth" : 5 * mm});
        }
    });
